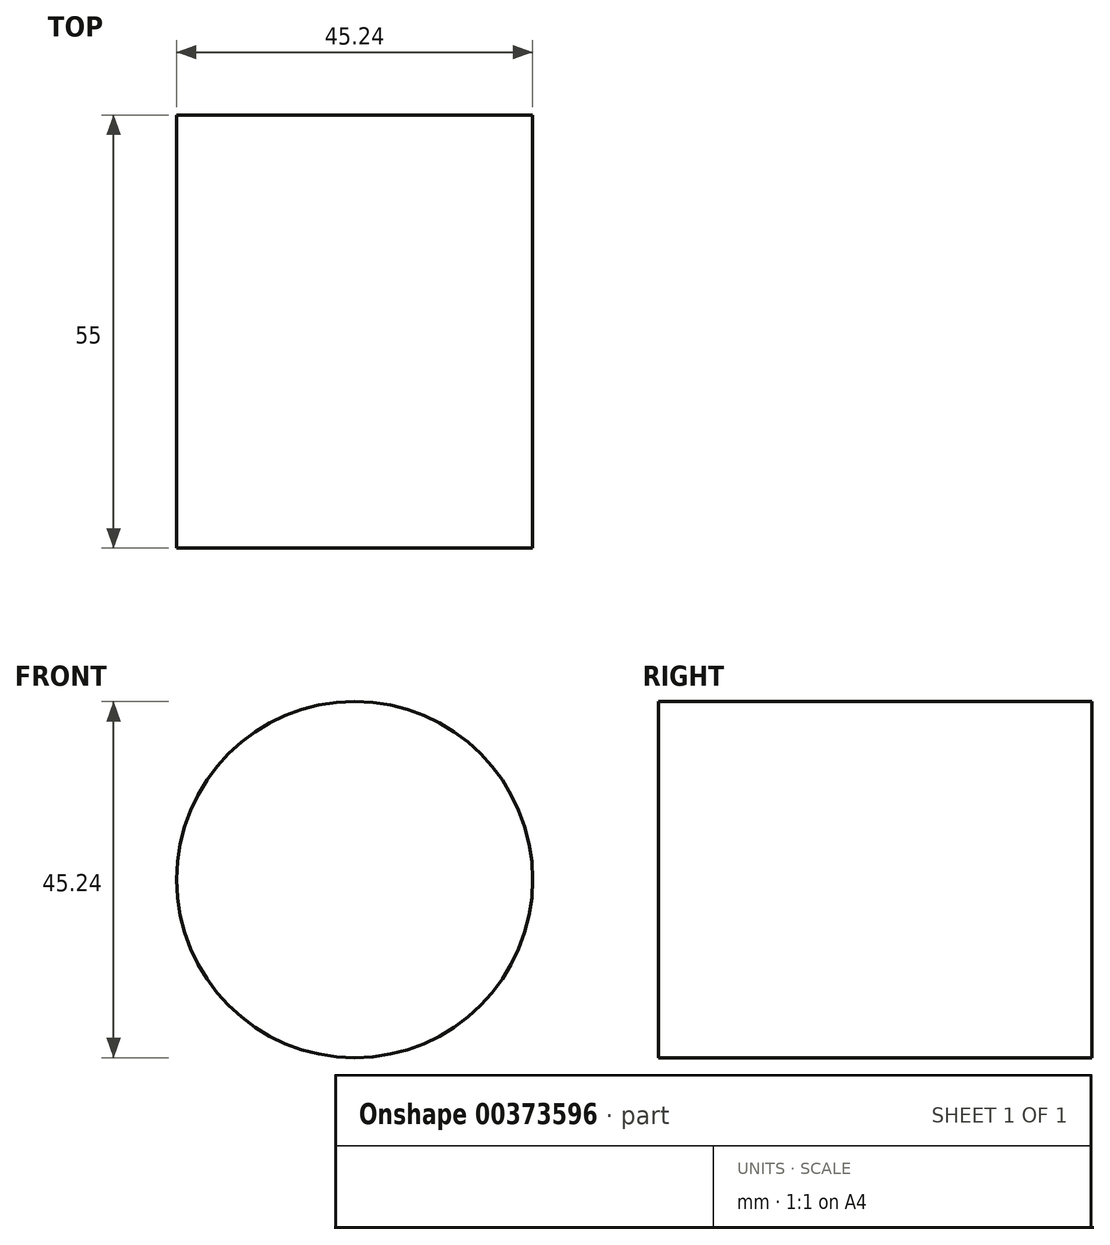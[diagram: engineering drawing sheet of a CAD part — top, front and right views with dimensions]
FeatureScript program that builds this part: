
annotation { "Feature Type Name" : "Feature", "Feature Type Description" : "" }
export const myFeature = defineFeature(function(context is Context, id is Id, definition is map)
    precondition{}
    {
        {
            var Q0;
            Q0=qCreatedBy(makeId("Top.planeOp"),FACE);
            var sketch = newSketch(context, id + "F0", { "sketchPlane" : qUnion([Q0])});
            skSolve(sketch);
        }
        {
            var Q0;
            Q0=qCreatedBy(makeId("Front.planeOp"),FACE);
            var sketch = newSketch(context, id + "F1", { "sketchPlane" : qUnion([Q0])});
            skCircle(sketch, "E0", {"center": v(-9.7, 16.88) * mm, "radius": 22.62 * mm});
            skSolve(sketch);
        }
        {
            var Q0;
            Q0 = qSketchRegion(id + "F0", true);
            var Q1;
            Q1=makeQuery(id+"F1.imprint","IMPRINT",FACE,{"disambiguationData":[TD([[makeQuery(id+"F1.imprint","IMPRINT",EDGE,{"derivedFrom":sQuery(id+"F1.wireOp",EDGE,"E0")}),1.0]])]});
            extrude(context, id + "F2", {"entities" : qUnion([Q0, Q1]), "depth" : 55 * mm});
        }
    });
